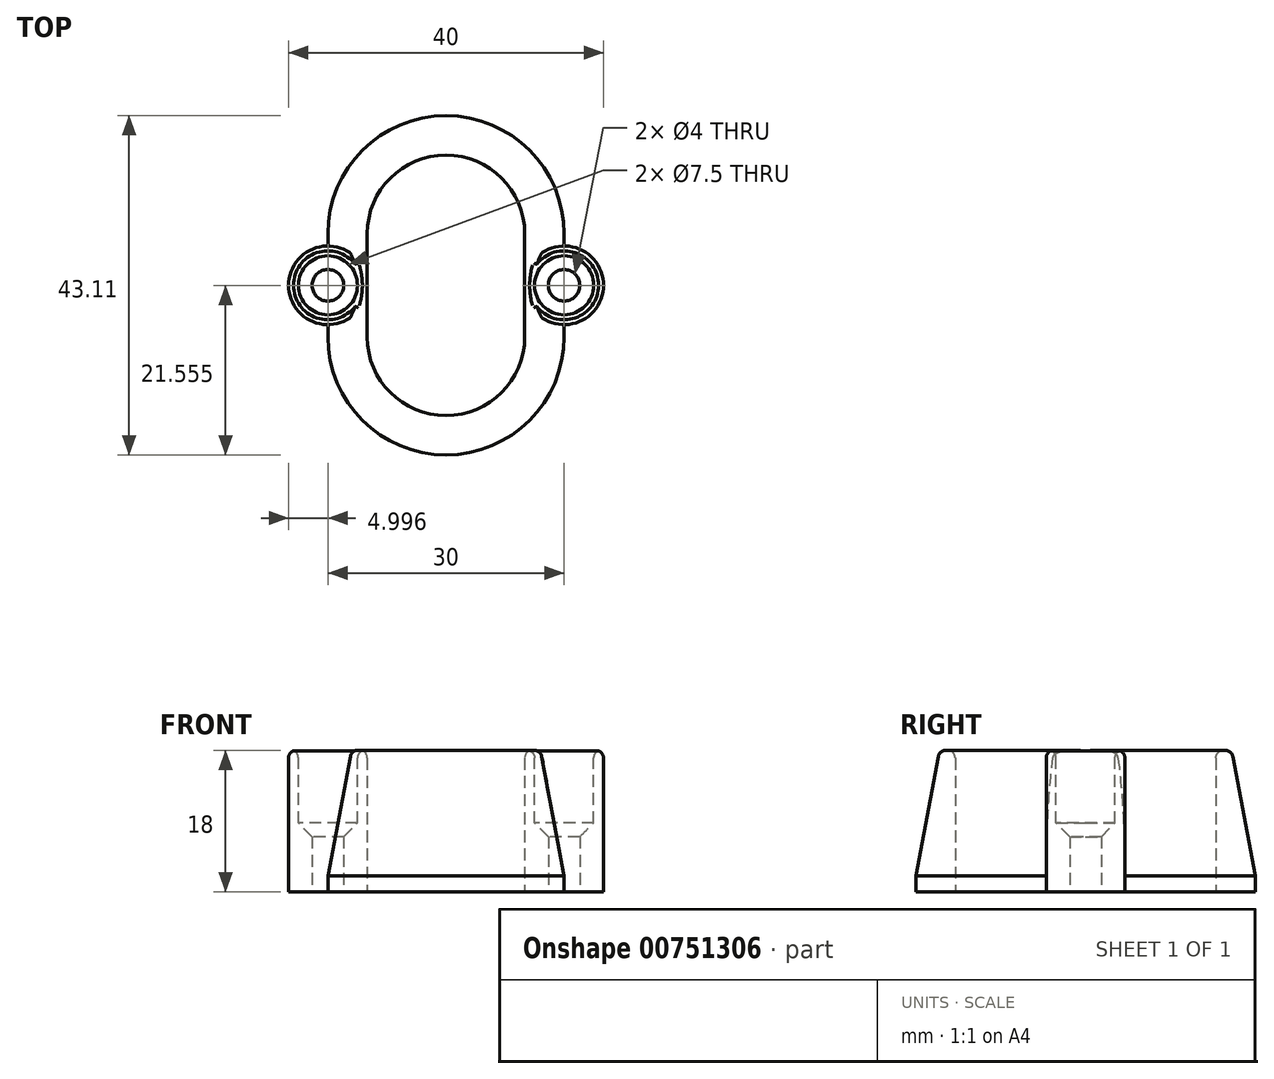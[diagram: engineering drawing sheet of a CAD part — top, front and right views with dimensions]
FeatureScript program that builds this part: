
annotation { "Feature Type Name" : "Feature", "Feature Type Description" : "" }
export const myFeature = defineFeature(function(context is Context, id is Id, definition is map)
    precondition{}
    {
        {
            var Q0;
            Q0=qCreatedBy(makeId("Top.planeOp"),FACE);
            var sketch = newSketch(context, id + "F0", { "sketchPlane" : qUnion([Q0])});
            skArc(sketch, "E0", {"start": v(-17.54, 27.72) * mm, "mid": v(-27.54, 37.72) * mm, "end": v(-37.54, 27.72) * mm});
            skArc(sketch, "E1", {"start": v(-37.54, 14.6) * mm, "mid": v(-27.54, 4.6) * mm, "end": v(-17.54, 14.6) * mm});
            skLineSegment(sketch, "E2", {"start": v(-17.54, 27.72) * mm, "end": v(-17.54, 14.6) * mm});
            skLineSegment(sketch, "E3", {"start": v(-37.54, 27.72) * mm, "end": v(-37.54, 14.6) * mm});
            skArc(sketch, "E4.0", {"start": v(-12.54, 27.72) * mm, "mid": v(-27.54, 42.72) * mm, "end": v(-42.54, 27.72) * mm});
            skLineSegment(sketch, "E4.1", {"start": v(-12.54, 27.72) * mm, "end": v(-12.54, 26.16) * mm});
            skArc(sketch, "E4.2", {"start": v(-42.54, 14.6) * mm, "mid": v(-27.54, -0.4) * mm, "end": v(-12.54, 14.6) * mm});
            skLineSegment(sketch, "E4.3", {"start": v(-42.54, 27.72) * mm, "end": v(-42.54, 26.16) * mm});
            skArc(sketch, "E5", {"start": v(-42.54, 26.16) * mm, "mid": v(-47.54, 21.16) * mm, "end": v(-42.54, 16.16) * mm});
            skArc(sketch, "E6", {"start": v(-12.54, 16.16) * mm, "mid": v(-7.54, 21.16) * mm, "end": v(-12.54, 26.16) * mm});
            skCircle(sketch, "E7", {"center": v(-42.54, 21.16) * mm, "radius": 2 * mm});
            skCircle(sketch, "E8", {"center": v(-12.54, 21.16) * mm, "radius": 2 * mm});
            skLineSegment(sketch, "E9.trimOffspring", {"start": v(-12.54, 16.16) * mm, "end": v(-12.54, 14.6) * mm});
            skLineSegment(sketch, "E10.trimOffspring", {"start": v(-42.54, 16.16) * mm, "end": v(-42.54, 14.6) * mm});
            skPoint(sketch, "E11.visualSharp", {"position": v(-42.54, 26.16) * mm});
            skLineSegment(sketch, "E11.filletArc", {"start": v(-42.54, 26.16) * mm, "end": v(-42.54, 26.16) * mm});
            skSolve(sketch);
        }
        {
            var Q0;
            Q0=makeQuery(id+"F0.imprint","IMPRINT",FACE,{"disambiguationData":[TD([[makeQuery(id+"F0.imprint","IMPRINT",EDGE,{"derivedFrom":sQuery(id+"F0.wireOp",EDGE,"E0")}),-1.0]])]});
            extrude(context, id + "F1", {"entities" : qUnion([Q0]), "depth" : 18 * mm, "offsetDistance" : 25 * mm});
        }
        {
            var Q0;
            Q0=makeQuery(id+"F1.opExtrude","CAP_EDGE",EDGE,{"disambiguationData":[OSD([sQuery(id+"F0.wireOp",EDGE,"E4.0")])],"isStart":false});
            var Q1;
            Q1=makeQuery(id+"F1.opExtrude","CAP_EDGE",EDGE,{"disambiguationData":[OSD([sQuery(id+"F0.wireOp",EDGE,"E4.3")])],"isStart":false});
            var Q2;
            Q2=makeQuery(id+"F1.opExtrude","CAP_EDGE",EDGE,{"disambiguationData":[OSD([sQuery(id+"F0.wireOp",EDGE,"E4.1")])],"isStart":false});
            var Q3;
            Q3=makeQuery(id+"F1.opExtrude","CAP_EDGE",EDGE,{"disambiguationData":[OSD([sQuery(id+"F0.wireOp",EDGE,"E4.2")])],"isStart":false});
            chamfer(context, id + "F2", {"entities" : qUnion([Q0, Q1, Q2, Q3]), "chamferType" : ChamferType.TWO_OFFSETS, "width1" : 3 * mm, "oppositeDirection" : false, "width2" : 16 * mm, "tangentPropagation" : true});
        }
        {
            var Q0;
            Q0=makeQuery(id+"F1.opExtrude","CAP_FACE",FACE,{"disambiguationData":[OSD([sQuery(id+"F0.wireOp",EDGE,"E0"),sQuery(id+"F0.wireOp",EDGE,"E1"),sQuery(id+"F0.wireOp",EDGE,"E2"),sQuery(id+"F0.wireOp",EDGE,"E3"),sQuery(id+"F0.wireOp",EDGE,"E4.0"),sQuery(id+"F0.wireOp",EDGE,"E4.1"),sQuery(id+"F0.wireOp",EDGE,"E4.2"),sQuery(id+"F0.wireOp",EDGE,"E4.3"),sQuery(id+"F0.wireOp",EDGE,"E5"),sQuery(id+"F0.wireOp",EDGE,"E6"),sQuery(id+"F0.wireOp",EDGE,"E7"),sQuery(id+"F0.wireOp",EDGE,"E8"),sQuery(id+"F0.wireOp",EDGE,"E9.trimOffspring"),sQuery(id+"F0.wireOp",EDGE,"E10.trimOffspring")])],"isStart":false});
            var sketch = newSketch(context, id + "F3", { "sketchPlane" : qUnion([Q0])});
            skCircle(sketch, "E12", {"center": v(-42.54, 21.16) * mm, "radius": 3.75 * mm});
            skCircle(sketch, "E13", {"center": v(-12.54, 21.16) * mm, "radius": 3.75 * mm});
            skSolve(sketch);
        }
        {
            var Q0;
            Q0 = qSketchRegion(id + "F3", true);
            extrude(context, id + "F4", {"entities" : qUnion([Q0]), "operationType" : NewBodyOperationType.REMOVE, "oppositeDirection" : true, "depth" : 8 * mm, "offsetDistance" : 25 * mm});
        }
        {
            var Q0;
            Q0=makeQuery(id+"F1.opExtrude","CAP_FACE",FACE,{"disambiguationData":[OSD([sQuery(id+"F0.wireOp",EDGE,"E0"),sQuery(id+"F0.wireOp",EDGE,"E1"),sQuery(id+"F0.wireOp",EDGE,"E2"),sQuery(id+"F0.wireOp",EDGE,"E3"),sQuery(id+"F0.wireOp",EDGE,"E4.0"),sQuery(id+"F0.wireOp",EDGE,"E4.1"),sQuery(id+"F0.wireOp",EDGE,"E4.2"),sQuery(id+"F0.wireOp",EDGE,"E4.3"),sQuery(id+"F0.wireOp",EDGE,"E5"),sQuery(id+"F0.wireOp",EDGE,"E6"),sQuery(id+"F0.wireOp",EDGE,"E7"),sQuery(id+"F0.wireOp",EDGE,"E8"),sQuery(id+"F0.wireOp",EDGE,"E9.trimOffspring"),sQuery(id+"F0.wireOp",EDGE,"E10.trimOffspring")])],"isStart":false});
            fillet(context, id + "F5", {"entities" : qUnion([Q0]), "radius" : 1 * mm, "tangentPropagation" : true, "allowEdgeOverflow" : false});
        }
        {
            var Q0;
            Q0=makeQuery(id+"F4.boolean.opBoolean","INTERSECT",EDGE,{"derivedFrom":[makeQuery(id+"F1.opExtrude","SWEPT_FACE",FACE,{"disambiguationData":[OSD([sQuery(id+"F0.wireOp",EDGE,"E7")])]}),makeQuery(id+"F4.opExtrude","CAP_FACE",FACE,{"disambiguationData":[OSD([sQuery(id+"F3.wireOp",EDGE,"E12")])],"isStart":false})]});
            var Q1;
            Q1=makeQuery(id+"F4.boolean.opBoolean","INTERSECT",EDGE,{"derivedFrom":[makeQuery(id+"F1.opExtrude","SWEPT_FACE",FACE,{"disambiguationData":[OSD([sQuery(id+"F0.wireOp",EDGE,"E8")])]}),makeQuery(id+"F4.opExtrude","CAP_FACE",FACE,{"disambiguationData":[OSD([sQuery(id+"F3.wireOp",EDGE,"E13")])],"isStart":false})]});
            chamfer(context, id + "F6", {"entities" : qUnion([Q0, Q1]), "width" : 3 * mm, "tangentPropagation" : true});
        }
    });
